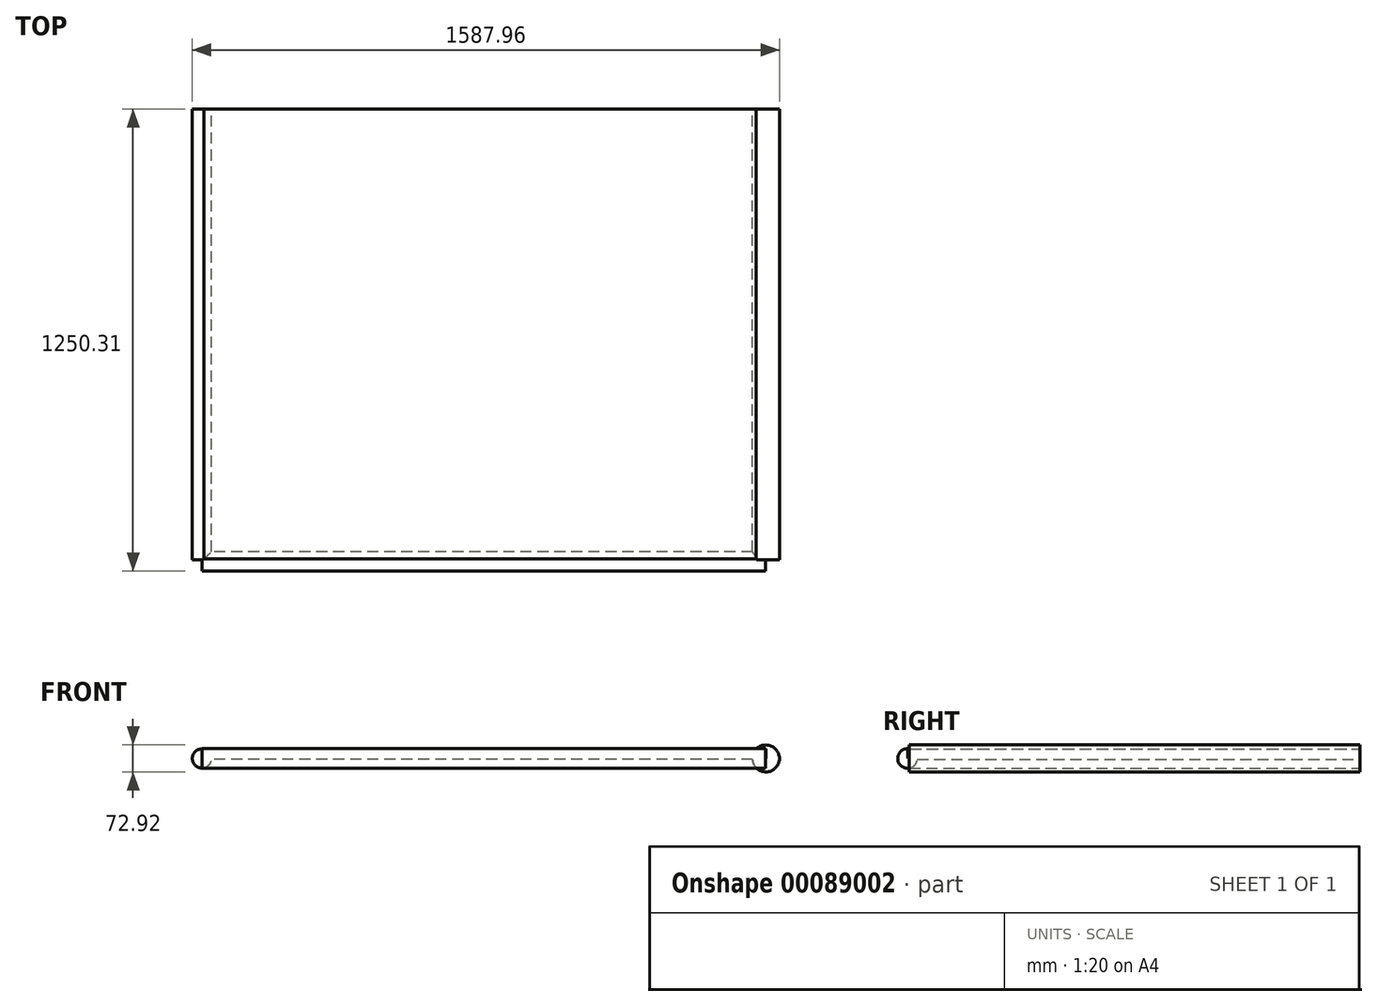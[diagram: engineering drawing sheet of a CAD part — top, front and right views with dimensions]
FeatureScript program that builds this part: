
annotation { "Feature Type Name" : "Feature", "Feature Type Description" : "" }
export const myFeature = defineFeature(function(context is Context, id is Id, definition is map)
    precondition{}
    {
        {
            var Q0;
            Q0=qCreatedBy(makeId("Right.planeOp"),FACE);
            var sketch = newSketch(context, id + "F0", { "sketchPlane" : qUnion([Q0])});
            skCircle(sketch, "E0", {"center": v(0, 0) * mm, "radius": 26.04 * mm});
            skSolve(sketch);
        }
        {
            var Q0;
            Q0=sQuery(id+"F0.wireOp",EDGE,"E0");
            extrude(context, id + "F1", {"bodyType" : ToolBodyType.SURFACE, "surfaceEntities" : qUnion([Q0]), "depth" : 1524 * mm});
        }
        {
            var Q0;
            Q0=qCreatedBy(makeId("Front.planeOp"),FACE);
            var sketch = newSketch(context, id + "F2", { "sketchPlane" : qUnion([Q0])});
            skCircle(sketch, "E1", {"center": v(0, 0) * mm, "radius": 26 * mm});
            skSolve(sketch);
        }
        {
            var Q0;
            Q0=makeQuery(id+"F2.imprint","IMPRINT",FACE,{"disambiguationData":[TD([[makeQuery(id+"F2.imprint","IMPRINT",EDGE,{"derivedFrom":sQuery(id+"F2.wireOp",EDGE,"E1")}),1.0]])]});
            extrude(context, id + "F3", {"entities" : qUnion([Q0]), "depth" : 1219.2 * mm});
        }
        {
            var Q0;
            Q0=qCreatedBy(makeId("Right.planeOp"),FACE);
            var sketch = newSketch(context, id + "F4", { "sketchPlane" : qUnion([Q0])});
            skCircle(sketch, "E2", {"center": v(-1223.82, 0) * mm, "radius": 26.48 * mm});
            skSolve(sketch);
        }
        {
            var Q0;
            Q0=makeQuery(id+"F4.imprint","IMPRINT",FACE,{"disambiguationData":[TD([[makeQuery(id+"F4.imprint","IMPRINT",EDGE,{"derivedFrom":sQuery(id+"F4.wireOp",EDGE,"E2")}),1.0]])]});
            extrude(context, id + "F5", {"entities" : qUnion([Q0]), "operationType" : NewBodyOperationType.ADD, "depth" : 1524 * mm});
        }
        {
            var Q0;
            Q0=qCreatedBy(makeId("Front.planeOp"),FACE);
            var sketch = newSketch(context, id + "F6", { "sketchPlane" : qUnion([Q0])});
            skCircle(sketch, "E3", {"center": v(1525.5, 0) * mm, "radius": 36.46 * mm});
            skSolve(sketch);
        }
        {
            var Q0;
            Q0=makeQuery(id+"F6.imprint","IMPRINT",FACE,{"disambiguationData":[TD([[makeQuery(id+"F6.imprint","IMPRINT",EDGE,{"derivedFrom":sQuery(id+"F6.wireOp",EDGE,"E3")}),1.0]])]});
            extrude(context, id + "F7", {"entities" : qUnion([Q0]), "operationType" : NewBodyOperationType.ADD, "depth" : 1219.2 * mm});
        }
        {
            var Q0;
            Q0=qCreatedBy(makeId("Top.planeOp"),FACE);
            var sketch = newSketch(context, id + "F8", { "sketchPlane" : qUnion([Q0])});
            skLineSegment(sketch, "E4.bottom", {"start": v(0, 0) * mm, "end": v(1525.44, 0) * mm});
            skLineSegment(sketch, "E4.top", {"start": v(0, -1222.8) * mm, "end": v(1525.44, -1222.8) * mm});
            skLineSegment(sketch, "E4.left", {"start": v(0, 0) * mm, "end": v(0, -1222.8) * mm});
            skLineSegment(sketch, "E4.right", {"start": v(1525.44, 0) * mm, "end": v(1525.44, -1222.8) * mm});
            skSolve(sketch);
        }
        {
            var Q0;
            Q0 = qSketchRegion(id + "F8", true);
            extrude(context, id + "F9", {"entities" : qUnion([Q0]), "operationType" : NewBodyOperationType.ADD, "depth" : 25.4 * mm});
        }
        {
            var Q0;
            Q0=qCreatedBy(makeId("Top.planeOp"),FACE);
            var sketch = newSketch(context, id + "F10", { "sketchPlane" : qUnion([Q0])});
            skCircle(sketch, "E5", {"center": v(0, -76) * mm, "radius": 25.35 * mm});
            skSolve(sketch);
        }
        {
            var Q0;
            Q0=sQuery(id+"F10.wireOp",EDGE,"E5");
            extrude(context, id + "F11", {"bodyType" : ToolBodyType.SURFACE, "surfaceEntities" : qUnion([Q0]), "depth" : 152.4 * mm});
        }
        {
            var Q0;
            Q0=qCreatedBy(makeId("Top.planeOp"),FACE);
            var sketch = newSketch(context, id + "F12", { "sketchPlane" : qUnion([Q0])});
            skCircle(sketch, "E6", {"center": v(0, -1181.1) * mm, "radius": 25.6 * mm});
            skSolve(sketch);
        }
        {
            var Q0;
            Q0=sQuery(id+"F12.wireOp",EDGE,"E6");
            extrude(context, id + "F13", {"bodyType" : ToolBodyType.SURFACE, "surfaceEntities" : qUnion([Q0]), "depth" : 152.4 * mm});
        }
        {
            var Q0;
            Q0=qCreatedBy(makeId("Top.planeOp"),FACE);
            var sketch = newSketch(context, id + "F14", { "sketchPlane" : qUnion([Q0])});
            skLineSegment(sketch, "E7.bottom", {"start": v(635.42, -174) * mm, "end": v(198.2, -174) * mm});
            skLineSegment(sketch, "E7.top", {"start": v(635.42, -439.45) * mm, "end": v(198.2, -439.45) * mm});
            skLineSegment(sketch, "E7.left", {"start": v(635.42, -174) * mm, "end": v(635.42, -439.45) * mm});
            skLineSegment(sketch, "E7.right", {"start": v(198.2, -174) * mm, "end": v(198.2, -439.45) * mm});
            skSolve(sketch);
        }
        {
            var Q0;
            {var subQ1=sQuery(id+"F2.wireOp",EDGE,"E1");var subQ2=sQuery(id+"F8.wireOp",EDGE,"E4.bottom");Q0=makeQuery(id+"F9.boolean.opBoolean","SPLIT",FACE,{"disambiguationData":[TD([makeQuery(id+"F3.opExtrude","SWEPT_FACE",FACE,{"disambiguationData":[OSD([subQ1])]})])],"derivedFrom":makeQuery(id+"F9.opExtrude","CAP_FACE",FACE,{"disambiguationData":[OSD([subQ2,sQuery(id+"F8.wireOp",EDGE,"E4.top"),sQuery(id+"F8.wireOp",EDGE,"E4.left"),sQuery(id+"F8.wireOp",EDGE,"E4.right")])],"isStart":false})});}
            extrude(context, id + "F15", {"entities" : qUnion([Q0]), "operationType" : NewBodyOperationType.ADD, "oppositeDirection" : true, "depth" : 27.78 * mm});
        }
        {
            var Q0;
            Q0=sQuery(id+"F14.wireOp",EDGE,"E7.right");
            var Q1;
            Q1=sQuery(id+"F14.wireOp",EDGE,"E7.bottom");
            var Q2;
            Q2=sQuery(id+"F14.wireOp",EDGE,"E7.left");
            var Q3;
            Q3=sQuery(id+"F14.wireOp",EDGE,"E7.top");
            extrude(context, id + "F16", {"bodyType" : ToolBodyType.SURFACE, "surfaceEntities" : qUnion([Q0, Q1, Q2, Q3]), "depth" : 64.4 * mm});
        }
        {
            var Q0;
            Q0=qCreatedBy(makeId("Top.planeOp"),FACE);
            var sketch = newSketch(context, id + "F17", { "sketchPlane" : qUnion([Q0])});
            skLineSegment(sketch, "E8.bottom", {"start": v(475.62, -1019.46) * mm, "end": v(118.62, -1019.46) * mm});
            skLineSegment(sketch, "E8.top", {"start": v(475.62, -812.54) * mm, "end": v(118.62, -812.54) * mm});
            skLineSegment(sketch, "E8.left", {"start": v(475.62, -1019.46) * mm, "end": v(475.62, -812.54) * mm});
            skLineSegment(sketch, "E8.right", {"start": v(118.62, -1019.46) * mm, "end": v(118.62, -812.54) * mm});
            skSolve(sketch);
        }
        {
            var Q0;
            Q0=sQuery(id+"F17.wireOp",EDGE,"E8.left");
            var Q1;
            Q1=sQuery(id+"F17.wireOp",EDGE,"E8.top");
            var Q2;
            Q2=sQuery(id+"F17.wireOp",EDGE,"E8.bottom");
            var Q3;
            Q3=sQuery(id+"F17.wireOp",EDGE,"E8.right");
            extrude(context, id + "F18", {"bodyType" : ToolBodyType.SURFACE, "surfaceEntities" : qUnion([Q0, Q1, Q2, Q3]), "depth" : 73.26 * mm});
        }
    });
